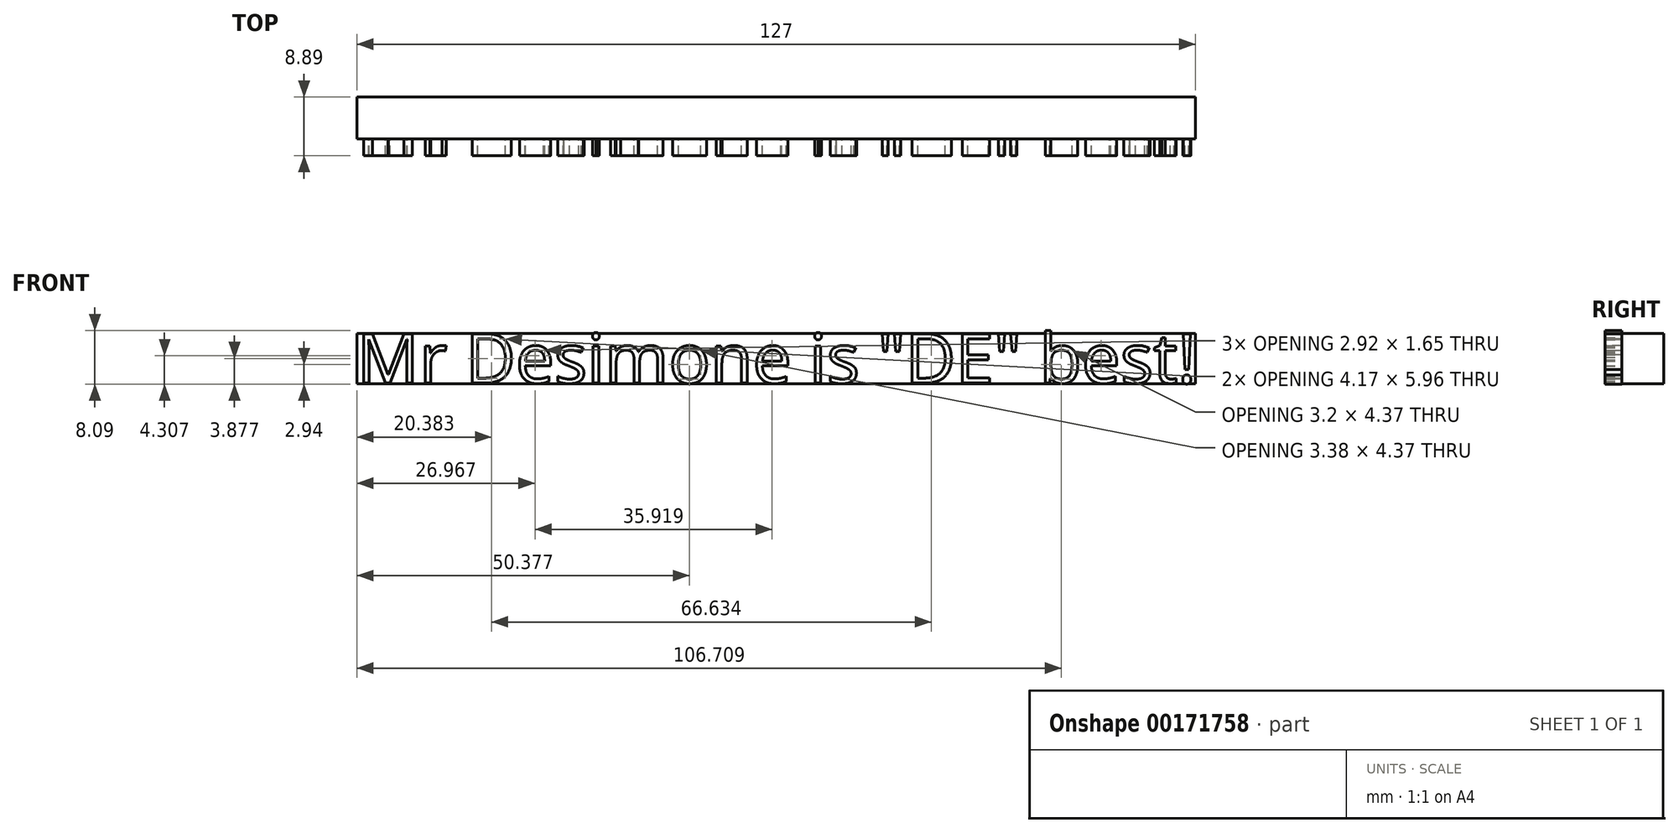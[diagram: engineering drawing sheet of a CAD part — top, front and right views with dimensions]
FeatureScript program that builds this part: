
annotation { "Feature Type Name" : "Feature", "Feature Type Description" : "" }
export const myFeature = defineFeature(function(context is Context, id is Id, definition is map)
    precondition{}
    {
        {
            var Q0;
            Q0=qCreatedBy(makeId("Front.planeOp"),FACE);
            var sketch = newSketch(context, id + "F0", { "sketchPlane" : qUnion([Q0])});
            skText(sketch, "E0", { "text": "Mr Desimone is \"DE\" best!", "fontName": "OpenSans-Regular.ttf"});
            const initialGuessF0  = {"E0": [0, -0.00752, 1, 0, 0.00752]};
            skSetInitialGuess(sketch, initialGuessF0);
            skSolve(sketch);
        }
        {
            var Q0;
            Q0 = qSketchRegion(id + "F0", true);
            extrude(context, id + "F1", {"entities" : qUnion([Q0]), "depth" : 2.54 * mm});
        }
        {
            var Q0;
            Q0=qCreatedBy(makeId("Front.planeOp"),FACE);
            var sketch = newSketch(context, id + "F2", { "sketchPlane" : qUnion([Q0])});
            skLineSegment(sketch, "E1.bottom", {"start": v(0, 0) * mm, "end": v(127, 0) * mm});
            skLineSegment(sketch, "E1.top", {"start": v(0, -7.62) * mm, "end": v(127, -7.62) * mm});
            skLineSegment(sketch, "E1.left", {"start": v(0, 0) * mm, "end": v(0, -7.62) * mm});
            skLineSegment(sketch, "E1.right", {"start": v(127, 0) * mm, "end": v(127, -7.62) * mm});
            skSolve(sketch);
        }
        {
            var Q0;
            Q0 = qSketchRegion(id + "F2", true);
            var Q1;
            Q1=makeQuery(id+"F2.imprint","IMPRINT",FACE,{"disambiguationData":[TD([[makeQuery(id+"F2.imprint","IMPRINT",EDGE,{"derivedFrom":sQuery(id+"F2.wireOp",EDGE,"E1.bottom")}),-1.0]])]});
            extrude(context, id + "F3", {"entities" : qUnion([Q0, Q1]), "oppositeDirection" : true, "depth" : 6.35 * mm});
        }
    });
